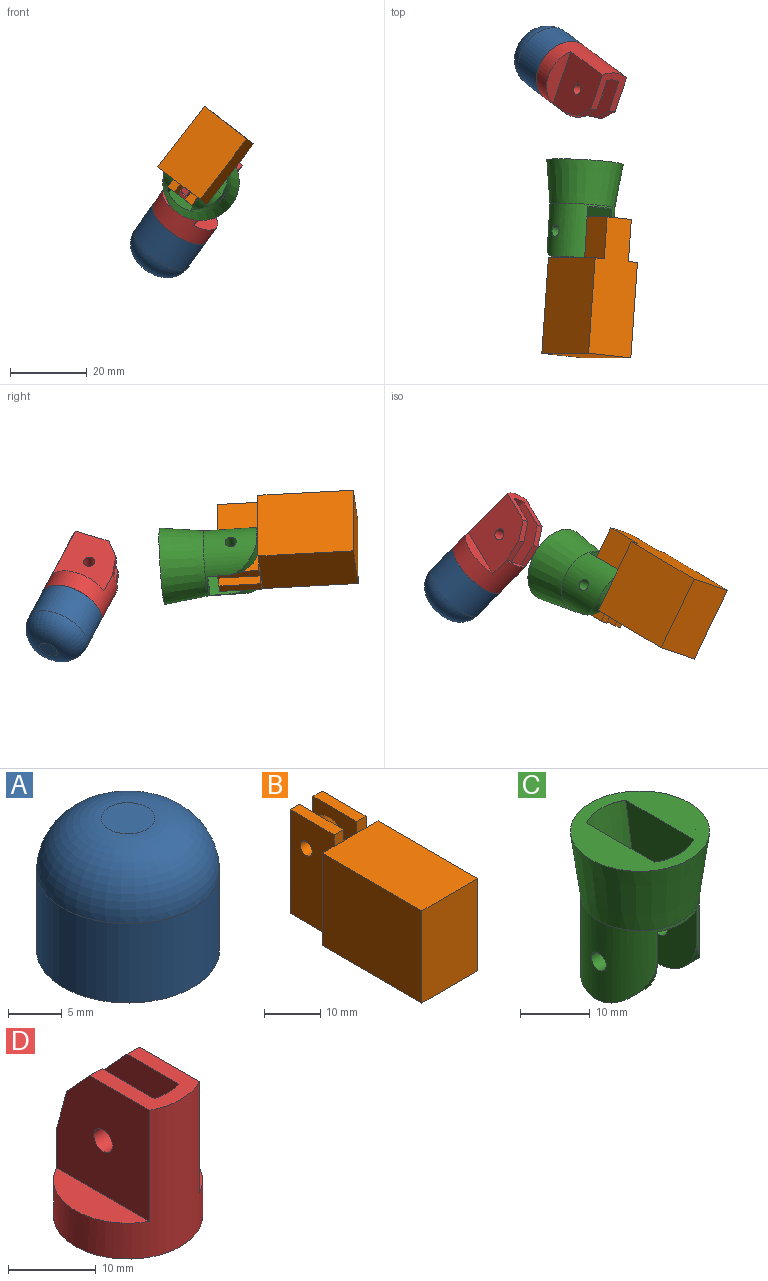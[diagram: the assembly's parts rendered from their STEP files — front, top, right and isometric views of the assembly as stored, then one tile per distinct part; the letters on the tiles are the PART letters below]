
ASSEMBLY  parts=4 mates=3
PART A: 7 faces, bbox 17x17x15 mm
  f0: cylinder r=8.5mm len=17mm, axis (0,0,-1), area 480.7mm2, adj f2,f3
  f1: plane 5x5mm, normal (0,0,1), area 19.6mm2, adj f3
  f2: plane 17x17mm, normal (0,0,-1), area 113.9mm2, adj f0,f4
  f3: torus R=2.5mm, axis (0,0,1), area 374.2mm2, adj f0,f1
  f4: cylinder r=6mm len=12mm, axis (0,0,-1), area 339.3mm2, adj f2,f6
  f5: plane 5x5mm, normal (0,0,-1), area 19.6mm2, adj f6
  f6: torus R=2.5mm, axis (0,0,1), area 163.3mm2, adj f4,f5
PART B: 22 faces, bbox 14x36x22.5 mm
  f0: plane 2.5x2.3mm, normal (0,-1,0), area 5.7mm2, adj f3,f4,f5,f13
  f1: plane 2.5x2.3mm, normal (0,-1,0), area 5.7mm2, adj f8,f9,f10,f13
  f2: plane 11x3.4mm, normal (0,0,1), area 37.4mm2, adj f3,f7,f8,f12
  f3: plane 12.7x11mm, normal (1,0,0), area 89.4mm2, adj f0,f2,f4,f7,f12,f20
  f4: plane 11x2.3mm, normal (0,0,1), area 25.3mm2, adj f0,f3,f5,f7
  f5: plane 22.5x11mm, normal (-1,0,0), area 240.4mm2, adj f0,f4,f6,f7,f17,f18
  f6: plane 36x14mm, normal (0,0,-1), area 438mm2, adj f5,f7,f10,f11,f14,f15,f16,f17
  f7: plane 22.5x8mm, normal (0,1,0), area 136.8mm2, adj f2,f3,f4,f5,f6,f8,f9,f10
  f8: plane 12.7x11mm, normal (-1,0,0), area 89.4mm2, adj f1,f2,f7,f9,f12,f21
  f9: plane 11x2.3mm, normal (0,0,1), area 25.3mm2, adj f1,f7,f8,f10
  f10: plane 22.5x11mm, normal (1,0,0), area 240.4mm2, adj f1,f6,f7,f9,f11,f18
  f11: plane 20x3mm, normal (0,1,0), area 60mm2, adj f6,f10,f13,f15
  f12: plane 10.2x3.4mm, normal (0,1,0), area 34.7mm2, adj f2,f3,f8,f13
  f13: plane 25x14mm, normal (0,0,1), area 350mm2, adj f0,f1,f11,f12,f14,f15,f16,f17
  f14: plane 25x20mm, normal (-1,0,0), area 500mm2, adj f6,f13,f16,f17
  f15: plane 25x20mm, normal (1,0,0), area 500mm2, adj f6,f11,f13,f16
  f16: plane 20x14mm, normal (0,-1,0), area 280mm2, adj f6,f13,f14,f15
  f17: plane 20x3mm, normal (0,1,0), area 60mm2, adj f5,f6,f13,f14
  f18: cylinder r=1.5mm len=8mm, axis (1,0,0), area 75.4mm2, adj f5,f10
  f19: cylinder r=2.5mm len=5mm, axis (1,0,0), area 6.3mm2, adj f20,f21
  f20: cone r=2.5mm half-angle=45deg, axis (-1,0,0), area 43.3mm2, adj f3,f19
  f21: cone r=2.5mm half-angle=45deg, axis (1,0,0), area 43.3mm2, adj f8,f19
PART C: 23 faces, bbox 20.1x20.1x25.6 mm
  f0: cone r=6.52mm half-angle=7.4deg, axis (0,0,1), area 98.1mm2, adj f1,f12,f14,f15
  f1: cone r=8.02mm half-angle=8.5deg, axis (0,0,-1), area 0.2mm2, adj f0,f14,f15,f18
  f2: cone r=8.02mm half-angle=8.5deg, axis (0,0,-1), area 0.2mm2, adj f3,f14,f15,f18
  f3: cone r=6.52mm half-angle=7.4deg, axis (0,0,1), area 98.1mm2, adj f2,f7,f14,f15
  f4: cylinder r=8mm len=8mm, axis (-1,0,0), area 28.2mm2, adj f5,f15,f16
  f5: plane 7x4.49mm, normal (0,0,-1), area 21.8mm2, adj f4,f15,f16
  f6: cylinder r=1.5mm len=4.5mm, axis (1,0,0), area 42.4mm2, adj f15,f16
  f7: cylinder r=6.5mm len=8mm, axis (0,0,-1), area 5.4mm2, adj f3,f8,f14,f15
  f8: plane 8x3.38mm, normal (0,0,-1), area 16.9mm2, adj f7,f14,f15,f16
  f9: plane 7x4.49mm, normal (0,0,-1), area 21.8mm2, adj f10,f14,f16
  f10: cylinder r=8mm len=8mm, axis (-1,0,0), area 28.2mm2, adj f9,f14,f16
  f11: plane 8x3.38mm, normal (0,0,-1), area 16.9mm2, adj f12,f14,f15,f16
  f12: cylinder r=6.5mm len=8mm, axis (0,0,-1), area 5.4mm2, adj f0,f11,f14,f15
  f13: cylinder r=1.5mm len=4.5mm, axis (1,0,0), area 42.3mm2, adj f14,f16
  f14: plane 25.62x15.12mm, normal (1,0,0), area 325.3mm2, adj f0,f1,f2,f3,f7,f8,f9,f10
  f15: plane 25.62x15.12mm, normal (-1,0,0), area 325.3mm2, adj f0,f1,f2,f3,f4,f5,f6,f7
  f16: cylinder r=8.5mm len=17mm, axis (0,0,-1), area 467.9mm2, adj f4,f5,f6,f8,f9,f10,f11,f13
  f17: cone r=8.5mm half-angle=7.4deg, axis (0,0,1), area 674mm2, adj f16,f18
  f18: plane 20x20mm, normal (0,0,1), area 192.1mm2, adj f1,f2,f14,f15,f17
  f19: cone r=8.02mm half-angle=8.5deg, axis (0,0,-1), area 0mm2, adj f20,f21
  f20: cylinder r=7.95mm len=0.01mm, axis (0,0,1), area 0mm2, adj f19,f21,f22
  f21: cone r=6.52mm half-angle=7.4deg, axis (0,0,1), area 0mm2, adj f19,f20,f22
  f22: plane 0x0mm, normal (0.79,0.62,0), area 0mm2, adj f20,f21
PART D: 24 faces, bbox 17x17x20.5 mm
  f0: cylinder r=6.5mm len=4.79mm, axis (0,0,1), area 19.2mm2, adj f9,f10,f12,f17
  f1: plane 8x1mm, normal (0,0,1), area 5.4mm2, adj f2,f13,f16,f17
  f2: cylinder r=8.5mm len=20.5mm, axis (0,0,-1), area 442mm2, adj f1,f3,f4,f5,f6,f7,f8
  f3: plane 10.67x8mm, normal (0,0,1), area 48.5mm2, adj f2,f6,f8,f9,f10,f11,f14,f15
  f4: plane 17x17mm, normal (0,0,-1), area 223.4mm2, adj f2,f21,f22
  f5: plane 15x4.5mm, normal (0,0,1), area 48.1mm2, adj f2,f6
  f6: plane 15.5x15mm, normal (1,0,0), area 206.5mm2, adj f2,f3,f5,f15,f16,f23
  f7: plane 15x4.5mm, normal (0,0,1), area 48.1mm2, adj f2,f8
  f8: plane 15.5x15mm, normal (-1,0,0), area 206.5mm2, adj f2,f3,f7,f13,f14,f23
  f9: plane 15.5x13.68mm, normal (-1,0,0), area 148.1mm2, adj f0,f3,f11,f12,f15,f16,f17,f19
  f10: plane 15.5x13.68mm, normal (1,0,0), area 148.1mm2, adj f0,f3,f11,f12,f13,f14,f17,f18
  f11: cylinder r=6.5mm len=15.5mm, axis (0,0,1), area 63mm2, adj f3,f9,f10,f12
  f12: plane 13x4mm, normal (0,0,1), area 47.6mm2, adj f0,f9,f10,f11,f21,f22
  f13: plane 5.91x2mm, normal (0,0.97,0.26), area 12.2mm2, adj f1,f8,f10,f14
  f14: plane 4.09x3.73mm, normal (0,0.74,0.67), area 11.1mm2, adj f3,f8,f10,f13
  f15: plane 4.09x3.73mm, normal (0,0.74,0.67), area 11.1mm2, adj f3,f6,f9,f16
  f16: plane 5.91x2mm, normal (0,0.97,0.26), area 12.2mm2, adj f1,f6,f9,f15
  f17: plane 4x1.32mm, normal (0,-0.58,0.82), area 5.4mm2, adj f0,f1,f9,f10
  f18: cone r=3.5mm half-angle=45deg, axis (-1,0,0), area 36.7mm2, adj f10,f20
  f19: cone r=3.5mm half-angle=45deg, axis (1,0,0), area 36.7mm2, adj f9,f20
  f20: cylinder r=2mm len=4mm, axis (1,0,0), area 12.6mm2, adj f18,f19
  f21: cylinder r=0.75mm len=5mm, axis (0,0,-1), area 23.6mm2, adj f4,f12
  f22: cylinder r=0.75mm len=5mm, axis (0,0,-1), area 23.6mm2, adj f4,f12
  f23: cylinder r=1.5mm len=8mm, axis (-1,0,0), area 75.4mm2, adj f6,f8
PLACE A rot(axis=(-0.94,0.11,0.31),159.2deg) t=(34.16,-15.9,61.58)mm
PLACE B rot(axis=(-0.04,-1,0.01),142.4deg) t=(-4.5,-14.25,11.16)mm fixed
PLACE C rot(axis=(-0.26,-0.7,-0.67),156.9deg) t=(-14.95,-25,-0.85)mm
PLACE D rot(axis=(0.31,-0.18,0.93),167.8deg) t=(-43.81,42.85,-48.05)mm
MATE revolute D.f23 <-> C.f14  axis (0.79,-0.09,-0.61) through (-9.16,18.77,-6.2)mm
MATE revolute C.f6 <-> B.f18  axis (0.79,-0.09,-0.61) through (-17.7,-17.88,1.13)mm
MATE fastened D.f2 <-> A.f0  axis (-0.53,0.4,-0.75) through (-18.96,24.12,-13.1)mm
